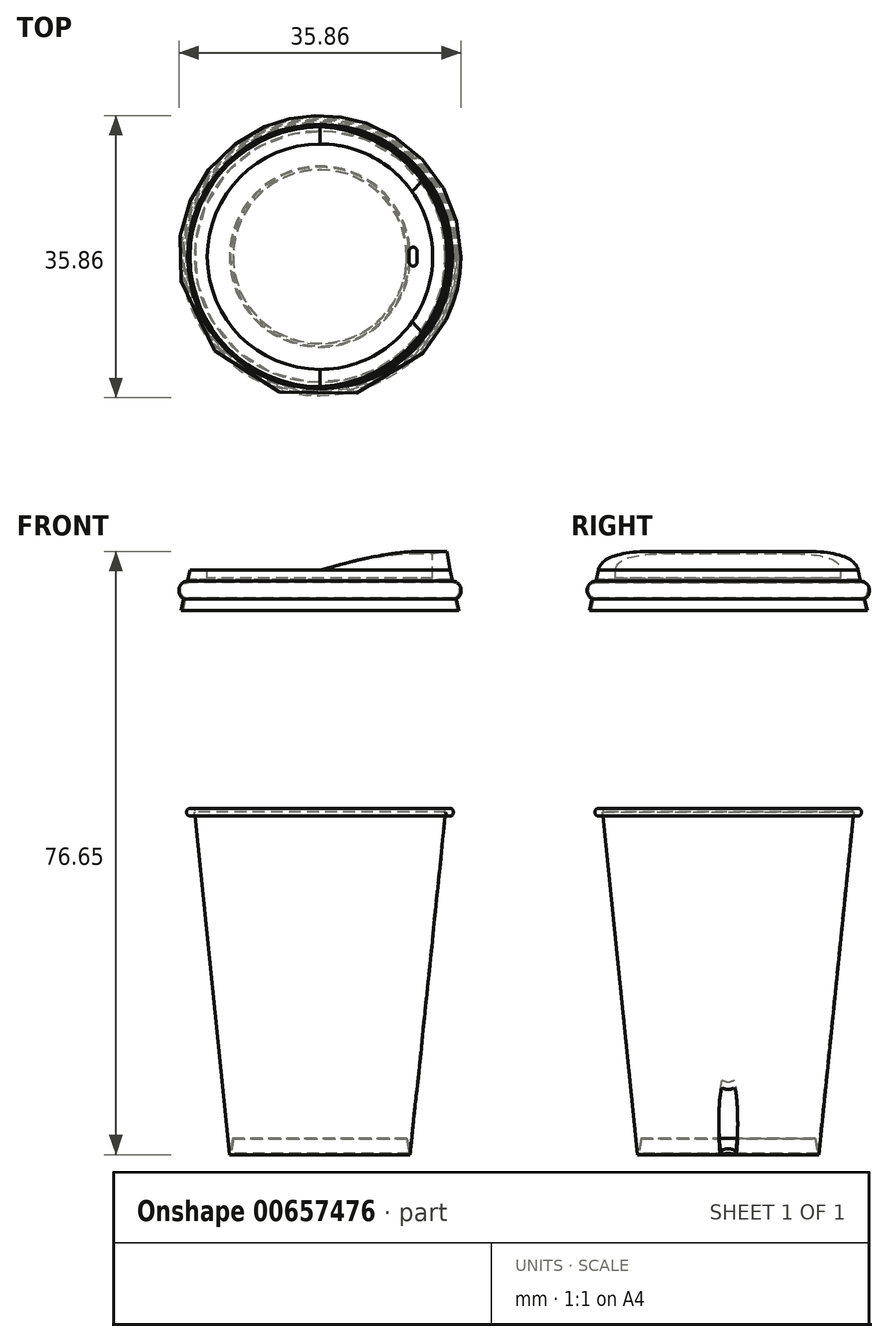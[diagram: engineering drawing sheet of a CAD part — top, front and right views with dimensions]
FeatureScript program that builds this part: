
annotation { "Feature Type Name" : "Feature", "Feature Type Description" : "" }
export const myFeature = defineFeature(function(context is Context, id is Id, definition is map)
    precondition{}
    {
        {
            var Q0;
            Q0=qCreatedBy(makeId("Front.planeOp"),FACE);
            var sketch = newSketch(context, id + "F0", { "sketchPlane" : qUnion([Q0])});
            skLineSegment(sketch, "E0", {"start": v(0, 17.96) * mm, "end": v(0, -19.71) * mm, "construction": true});
            skLineSegment(sketch, "E1", {"start": v(16, -19.83) * mm, "end": v(11.5, -63.83) * mm});
            skLineSegment(sketch, "E2", {"start": v(11.5, -63.83) * mm, "end": v(11.35, -63.83) * mm});
            skCircle(sketch, "E3", {"center": v(16.45, -20.33) * mm, "radius": 0.5 * mm});
            skLineSegment(sketch, "E4", {"start": v(16, -19.83) * mm, "end": v(16.45, -19.83) * mm});
            skLineSegment(sketch, "E5", {"start": v(11, -61.84) * mm, "end": v(0, -61.84) * mm});
            skLineSegment(sketch, "E6", {"start": v(11, -61.84) * mm, "end": v(11.35, -63.83) * mm});
            skLineSegment(sketch, "E7.0", {"start": v(11.08, -61.74) * mm, "end": v(0, -61.74) * mm});
            skLineSegment(sketch, "E7.1", {"start": v(11.08, -61.74) * mm, "end": v(11.42, -63.64) * mm});
            skLineSegment(sketch, "E7.2", {"start": v(15.9, -19.83) * mm, "end": v(11.42, -63.64) * mm});
            skLineSegment(sketch, "E8", {"start": v(0, -61.84) * mm, "end": v(0, -61.74) * mm});
            skLineSegment(sketch, "E9", {"start": v(16, -19.83) * mm, "end": v(15.9, -19.83) * mm});
            skSolve(sketch);
        }
        {
            var Q0;
            Q0 = qSketchRegion(id + "F0", true);
            var Q1;
            Q1=sQuery(id+"F0.wireOp",EDGE,"E0");
            revolve(context, id + "F1", {"entities" : qUnion([Q0]), "axis" : qUnion([Q1]), "revolveType" : RevolveType.FULL});
        }
        {
            var Q0;
            Q0=qCreatedBy(makeId("Front.planeOp"),FACE);
            var sketch = newSketch(context, id + "F2", { "sketchPlane" : qUnion([Q0])});
            skLineSegment(sketch, "E10", {"start": v(0, 23.25) * mm, "end": v(0, 4.03) * mm, "construction": true});
            skLineSegment(sketch, "E11", {"start": v(17.65, 5.28) * mm, "end": v(17.31, 6.78) * mm});
            skLineSegment(sketch, "E12", {"start": v(16.5, 10.4) * mm, "end": v(0, 10.4) * mm});
            skArc(sketch, "E13", {"start": v(17.31, 6.78) * mm, "mid": v(17.9, 8.1) * mm, "end": v(16.8, 9.04) * mm});
            skLineSegment(sketch, "E14.trimOffspring", {"start": v(16.8, 9.04) * mm, "end": v(16.5, 10.4) * mm});
            skLineSegment(sketch, "E15.0", {"start": v(16.56, 9.21) * mm, "end": v(0, 9.2) * mm});
            skLineSegment(sketch, "E15.1", {"start": v(16.65, 8.84) * mm, "end": v(16.56, 9.21) * mm});
            skArc(sketch, "E15.2", {"start": v(17.08, 6.9) * mm, "mid": v(17.7, 8.06) * mm, "end": v(16.65, 8.84) * mm});
            skLineSegment(sketch, "E15.3", {"start": v(17.45, 5.28) * mm, "end": v(17.08, 6.9) * mm});
            skLineSegment(sketch, "E16", {"start": v(0, 9.2) * mm, "end": v(0, 10.4) * mm});
            skLineSegment(sketch, "E17", {"start": v(17.45, 5.28) * mm, "end": v(17.65, 5.28) * mm});
            skLineSegment(sketch, "E18", {"start": v(16.5, 10.4) * mm, "end": v(16.15, 12.82) * mm});
            skLineSegment(sketch, "E19", {"start": v(16.15, 12.82) * mm, "end": v(14.32, 12.52) * mm});
            skLineSegment(sketch, "E20", {"start": v(14.32, 12.52) * mm, "end": v(14.32, 10.4) * mm});
            skLineSegment(sketch, "E21", {"start": v(16.56, 9.21) * mm, "end": v(16.5, 10.4) * mm});
            skSolve(sketch);
        }
        {
            var Q0;
            Q0=makeQuery(id+"F2.imprint","IMPRINT",FACE,{"disambiguationData":[TD([[makeQuery(id+"F2.imprint","IMPRINT",EDGE,{"derivedFrom":sQuery(id+"F2.wireOp",EDGE,"E11")}),1.0]])]});
            var Q1;
            Q1=makeQuery(id+"F2.imprint","IMPRINT",FACE,{"disambiguationData":[TD([[makeQuery(id+"F2.imprint","IMPRINT",EDGE,{"derivedFrom":sQuery(id+"F2.wireOp",EDGE,"E15.0")}),-1.0]])]});
            var Q2;
            Q2=sQuery(id+"F2.wireOp",EDGE,"E10");
            revolve(context, id + "F3", {"entities" : qUnion([Q0, Q1]), "axis" : qUnion([Q2]), "revolveType" : RevolveType.FULL});
        }
        {
            var Q0;
            {var subQ0=sQuery(id+"F2.wireOp",EDGE,"E18");Q0=makeQuery(id+"F2.imprint","IMPRINT",FACE,{"disambiguationData":[TD([[makeQuery(id+"F2.imprint","IMPRINT",EDGE,{"derivedFrom":subQ0}),1.0]])]});}
            var Q1;
            Q1=sQuery(id+"F2.wireOp",EDGE,"E10");
            revolve(context, id + "F4", {"operationType" : NewBodyOperationType.ADD, "entities" : qUnion([Q0]), "axis" : qUnion([Q1]), "revolveType" : RevolveType.TWO_DIRECTIONS, "angle" : 90 * degree, "angleBack" : 270 * degree});
        }
        {
            var Q0;
            Q0=makeQuery(id+"F4.opRevolve","CAP_EDGE",EDGE,{"disambiguationData":[OSD([sQuery(id+"F2.wireOp",EDGE,"E19")])],"isStart":false});
            var Q1;
            Q1=makeQuery(id+"F4.opRevolve","CAP_EDGE",EDGE,{"disambiguationData":[OSD([sQuery(id+"F2.wireOp",EDGE,"E19")])],"isStart":true});
            fillet(context, id + "F5", {"entities" : qUnion([Q0, Q1]), "radius" : 80 * mm, "tangentPropagation" : true, "allowEdgeOverflow" : false});
        }
        {
            var Q0;
            Q0=makeQuery(id+"F3.opRevolve","SWEPT_FACE",FACE,{"disambiguationData":[OSD([sQuery(id+"F2.wireOp",EDGE,"E12")])]});
            var sketch = newSketch(context, id + "F6", { "sketchPlane" : qUnion([Q0])});
            skCircle(sketch, "E22", {"center": v(0, 0) * mm, "radius": 14.32 * mm});
            skSolve(sketch);
        }
        {
            var Q0;
            Q0 = qSketchRegion(id + "F6", true);
            extrude(context, id + "F7", {"entities" : qUnion([Q0]), "operationType" : NewBodyOperationType.REMOVE, "oppositeDirection" : true, "depth" : 1 * mm, "offsetDistance" : 25 * mm});
        }
        {
            var Q0;
            Q0=makeQuery(id+"F7.boolean.opBoolean","COPY",FACE,{"derivedFrom":makeQuery(id+"F7.opExtrude","CAP_FACE",FACE,{"disambiguationData":[OSD([sQuery(id+"F6.wireOp",EDGE,"E22")])],"isStart":false})});
            var sketch = newSketch(context, id + "F8", { "sketchPlane" : qUnion([Q0])});
            skArc(sketch, "E23", {"start": v(12.35, 0.7) * mm, "mid": v(11.83, 1.2) * mm, "end": v(11.32, 0.7) * mm});
            skLineSegment(sketch, "E24", {"start": v(11.32, 0.7) * mm, "end": v(11.32, -0.7) * mm});
            skLineSegment(sketch, "E25", {"start": v(12.35, 0.7) * mm, "end": v(12.35, -0.7) * mm});
            skArc(sketch, "E26", {"start": v(11.32, -0.7) * mm, "mid": v(11.83, -1.2) * mm, "end": v(12.35, -0.7) * mm});
            skPoint(sketch, "E27", {"position": v(11.32, 0) * mm});
            skSolve(sketch);
        }
        {
            var Q0;
            Q0 = qSketchRegion(id + "F8", true);
            extrude(context, id + "F9", {"entities" : qUnion([Q0]), "operationType" : NewBodyOperationType.REMOVE, "endBound" : BoundingType.THROUGH_ALL, "oppositeDirection" : true, "depth" : 25 * mm, "offsetDistance" : 25 * mm});
        }
    });
